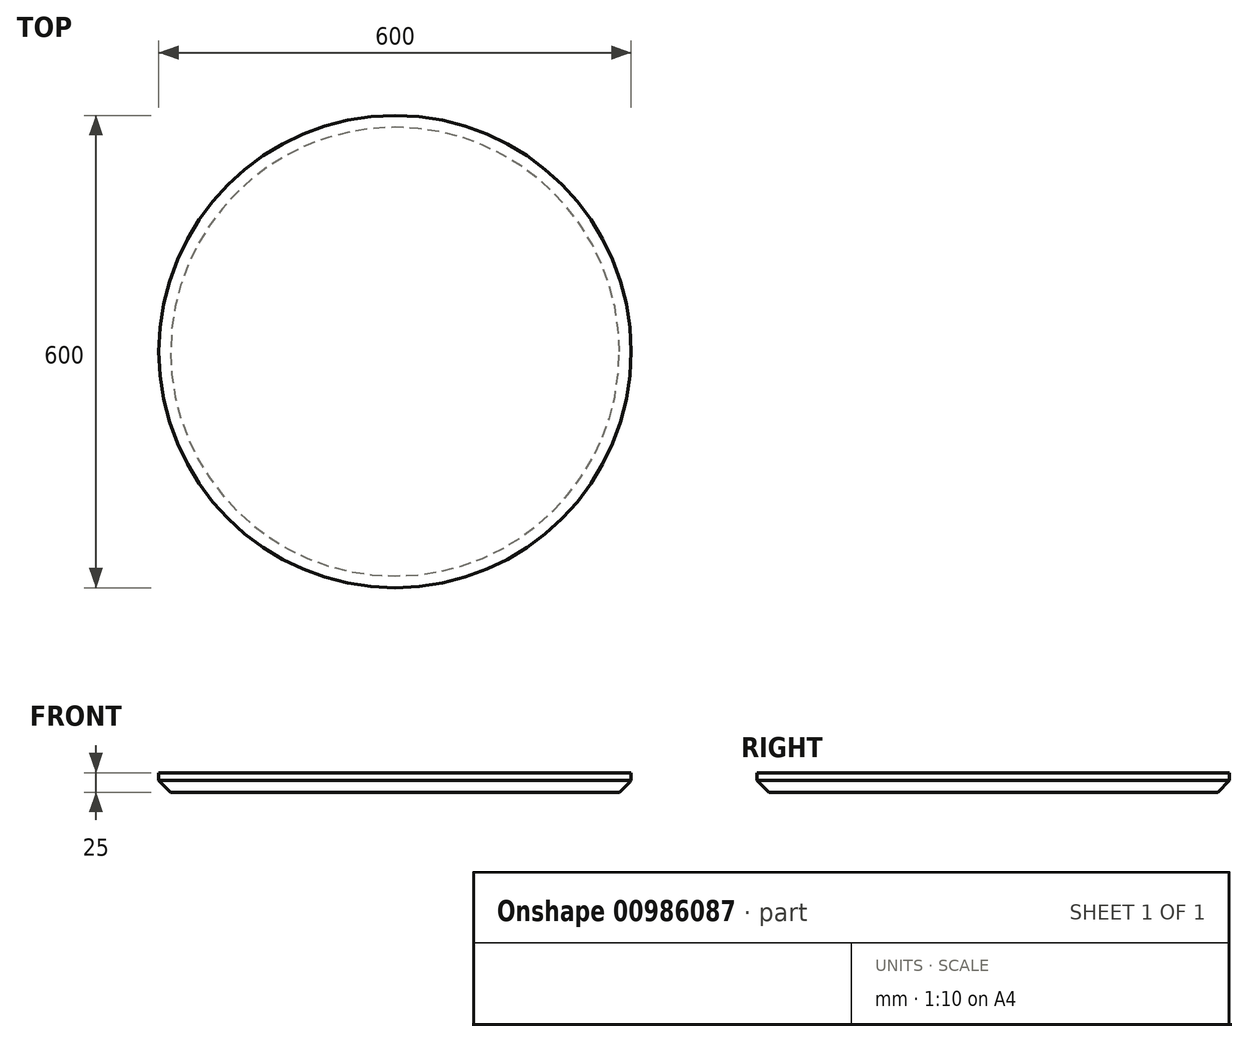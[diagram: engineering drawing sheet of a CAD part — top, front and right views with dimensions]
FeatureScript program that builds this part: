
annotation { "Feature Type Name" : "Feature", "Feature Type Description" : "" }
export const myFeature = defineFeature(function(context is Context, id is Id, definition is map)
    precondition{}
    {
        {
            var Q0;
            Q0=qCreatedBy(makeId("Top.planeOp"),FACE);
            var sketch = newSketch(context, id + "F0", { "sketchPlane" : qUnion([Q0])});
            skCircle(sketch, "E0", {"center": v(0, 0) * mm, "radius": 300 * mm});
            skSolve(sketch);
        }
        {
            var Q0;
            Q0 = qSketchRegion(id + "F0", true);
            extrude(context, id + "F1", {"entities" : qUnion([Q0]), "depth" : 25 * mm, "offsetDistance" : 25 * mm});
        }
        {
            var Q0;
            Q0=makeQuery(id+"F1.opExtrude","CAP_FACE",FACE,{"disambiguationData":[OSD([sQuery(id+"F0.wireOp",EDGE,"E0")])],"isStart":true});
            chamfer(context, id + "F2", {"entities" : qUnion([Q0]), "width" : 15 * mm, "tangentPropagation" : true});
        }
    });
